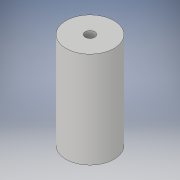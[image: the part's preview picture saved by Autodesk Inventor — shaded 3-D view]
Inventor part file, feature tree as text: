
AUTODESK INVENTOR PART (.ipt)
format: ipt  version: 2019 (Build 230136000, 136)  size: 100,864 bytes
history: native  units: mm
features: sketch x2, other x1, extrude x1, hole x1
ambient origin geometry x8: Origin, YZ Plane, XZ Plane, XY Plane, X Axis, Y Axis, Z Axis, Center Point
bodies: Body1 (feature_tree)
feature tree (5):
  other  "ソリッド1"
  extrude  "押し出し1"  Depth=30.0mm
  hole  "穴1"  [1 undecoded]
  sketch  "スケッチ1"
  sketch  "スケッチ2"
note: 1 required parameter value undecoded (feature->parameter linkage not recoverable at this tier; creation-order binding heuristic only, values carry confidence <= 0.55)
